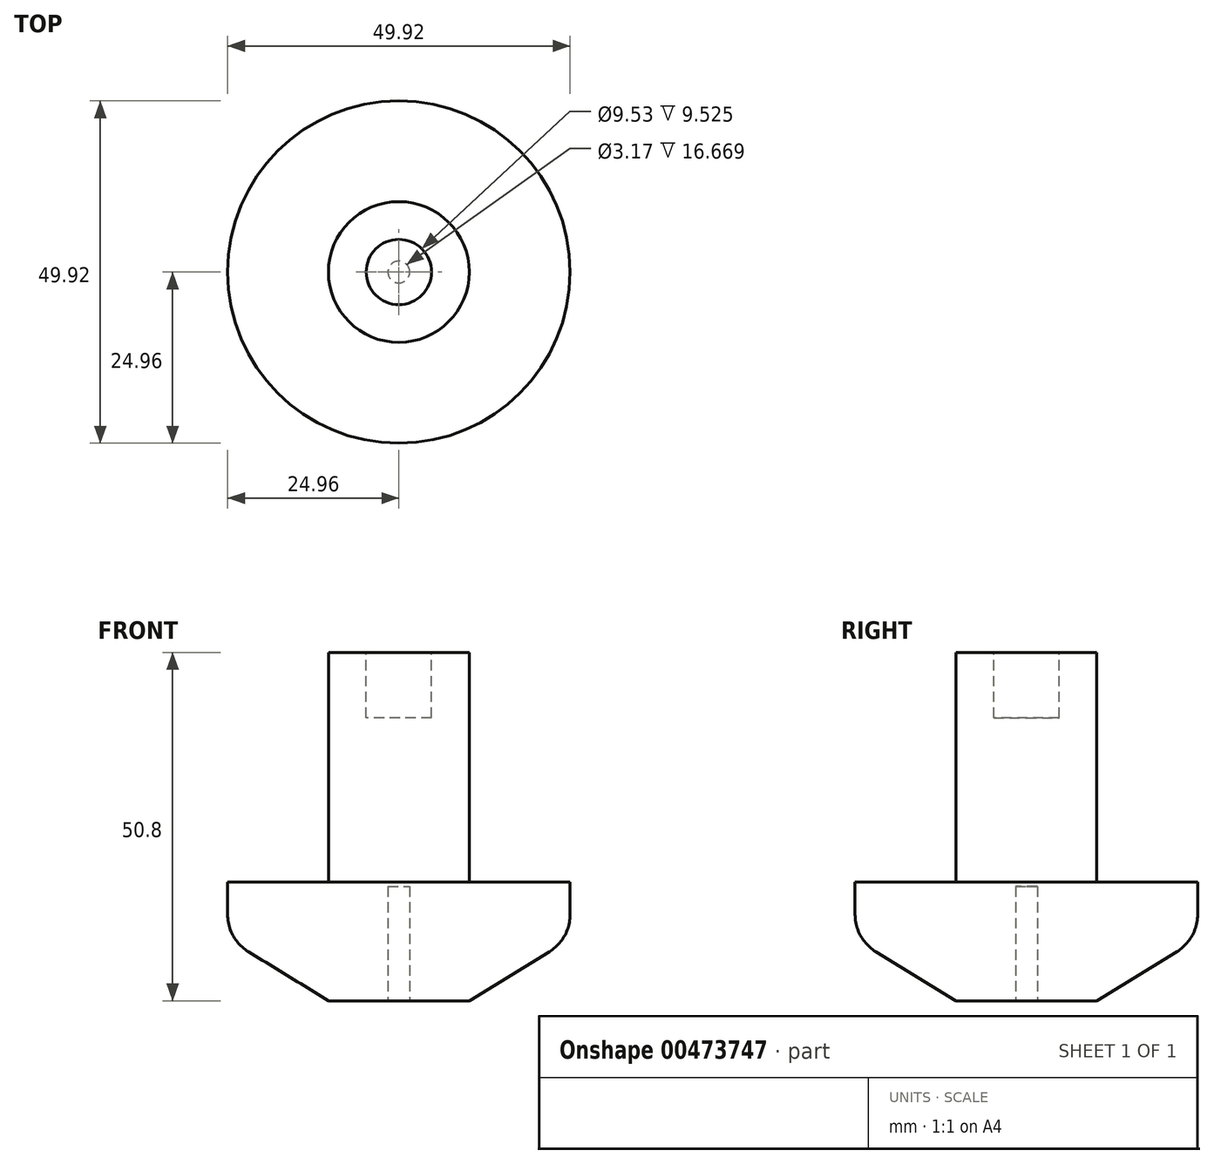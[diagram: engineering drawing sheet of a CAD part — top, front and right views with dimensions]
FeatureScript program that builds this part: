
annotation { "Feature Type Name" : "Feature", "Feature Type Description" : "" }
export const myFeature = defineFeature(function(context is Context, id is Id, definition is map)
    precondition{}
    {
        {
            var Q0;
            Q0=qCreatedBy(makeId("Front.planeOp"),FACE);
            var sketch = newSketch(context, id + "F0", { "sketchPlane" : qUnion([Q0])});
            skLineSegment(sketch, "E0", {"start": v(0, 0) * mm, "end": v(0, 50.8) * mm});
            skLineSegment(sketch, "E1", {"start": v(0, 0) * mm, "end": v(10.26, 0) * mm});
            skLineSegment(sketch, "E2", {"start": v(10.26, 0) * mm, "end": v(21.93, 7.15) * mm});
            skLineSegment(sketch, "E3", {"start": v(24.96, 12.57) * mm, "end": v(24.96, 17.33) * mm});
            skLineSegment(sketch, "E4", {"start": v(24.96, 17.33) * mm, "end": v(10.26, 17.33) * mm});
            skLineSegment(sketch, "E5", {"start": v(10.26, 17.33) * mm, "end": v(10.26, 50.8) * mm});
            skLineSegment(sketch, "E6", {"start": v(10.26, 50.8) * mm, "end": v(0, 50.8) * mm});
            skPoint(sketch, "E7.visualSharp", {"position": v(24.96, 9.01) * mm});
            skArc(sketch, "E7.filletArc", {"start": v(21.93, 7.15) * mm, "mid": v(24.15, 9.47) * mm, "end": v(24.96, 12.57) * mm});
            skSolve(sketch);
        }
        {
            var Q0;
            Q0=makeQuery(id+"F0.imprint","IMPRINT",FACE,{"disambiguationData":[TD([[makeQuery(id+"F0.imprint","IMPRINT",EDGE,{"derivedFrom":sQuery(id+"F0.wireOp",EDGE,"E0")}),-1.0]])]});
            var Q1;
            Q1=sQuery(id+"F0.wireOp",EDGE,"E0");
            revolve(context, id + "F1", {"entities" : qUnion([Q0]), "axis" : qUnion([Q1]), "revolveType" : RevolveType.FULL});
        }
        {
            var Q0;
            Q0=makeQuery(id+"F1.opRevolve","SWEPT_FACE",FACE,{"disambiguationData":[OSD([sQuery(id+"F0.wireOp",EDGE,"E6")])]});
            var sketch = newSketch(context, id + "F2", { "sketchPlane" : qUnion([Q0])});
            skCircle(sketch, "E8", {"center": v(0, 0) * mm, "radius": 4.76 * mm});
            skSolve(sketch);
        }
        {
            var Q0;
            Q0=makeQuery(id+"F2.imprint","IMPRINT",FACE,{"disambiguationData":[TD([[makeQuery(id+"F2.imprint","IMPRINT",EDGE,{"derivedFrom":sQuery(id+"F2.wireOp",EDGE,"E8")}),1.0]])]});
            extrude(context, id + "F3", {"entities" : qUnion([Q0]), "operationType" : NewBodyOperationType.REMOVE, "oppositeDirection" : true, "depth" : 9.52 * mm});
        }
        {
            var Q0;
            Q0=makeQuery(id+"F1.opRevolve","SWEPT_FACE",FACE,{"disambiguationData":[OSD([sQuery(id+"F0.wireOp",EDGE,"E1")])]});
            var sketch = newSketch(context, id + "F4", { "sketchPlane" : qUnion([Q0])});
            skCircle(sketch, "E9", {"center": v(0, 0) * mm, "radius": 1.59 * mm});
            skSolve(sketch);
        }
        {
            var Q0;
            Q0=qSketchRegion(id+"F4",true);
            extrude(context, id + "F5", {"entities" : qUnion([Q0]), "operationType" : NewBodyOperationType.REMOVE, "oppositeDirection" : true, "depth" : 16.67 * mm});
        }
    });
